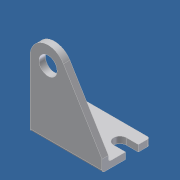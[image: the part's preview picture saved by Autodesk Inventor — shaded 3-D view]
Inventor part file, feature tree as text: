
AUTODESK INVENTOR PART (.ipt)
format: ipt  version: unknown  size: 207,360 bytes
history: native  units: in
note: dims shown in document units (in); Inventor stores cm internally (conversion verified against a paired STEP export)
features: other x14, extrude x8, sketch x8
ambient origin geometry x8: Origin, YZ Plane, XZ Plane, XY Plane, X Axis, Y Axis, Z Axis, Center Point
feature tree (30):
  extrude  "Extrusion1"  Depth=1.0in TaperAngle=0.0deg
  extrude  "Extrusion2"  Depth=0.1345in TaperAngle=0.0deg
  extrude  "Extrusion3"  Depth=0.1345in TaperAngle=0.0deg
  extrude  "Extrusion4"  Depth=0.1345in TaperAngle=0.0deg
  extrude  "Extrusion5"  [1 undecoded]
  sketch  "Sketch_6"
  sketch  "Sketch_7"
  extrude  "Extrusion6"  [1 undecoded]
  extrude  "Extrusion7"  [1 undecoded]
  extrude  "Extrusion8"  [1 undecoded]
  other  "to_dummy_R_XY"
  other  "to_dummy_R_YZ"
  other  "to_dummy_R_ZX"
  other  "to_dummy_R_X"
  other  "to_dummy_R_Y"
  other  "to_dummy_R_Z"
  other  "to_dummy_R_Center"
  other  "to_pin_R_XY"
  other  "to_pin_R_YZ"
  other  "to_pin_R_ZX"
  other  "to_pin_R_X"
  other  "to_pin_R_Y"
  other  "to_pin_R_Z"
  other  "to_pin_R_Center"
  sketch  "Sketch_1"  dims[d0=1.5in d1=0.0in d2=1.0in d3=0.0in]
  sketch  "Sketch_2"  dims[d4=0.1345in d5=0.0in d6=0.1345in d7=0.0in]
  sketch  "Sketch_3"  dims[d8=0.1345in d9=0.0in d10=0.1345in d11=0.0in]
  sketch  "Sketch_4"  dims[d12=0.1345in d13=0.0in d14=0.1345in d15=0.0in]
  sketch  "Sketch_5"
  sketch  "Sketch_8"
note: 4 required parameter values undecoded (feature->parameter linkage not recoverable at this tier; creation-order binding heuristic only, values carry confidence <= 0.55)
